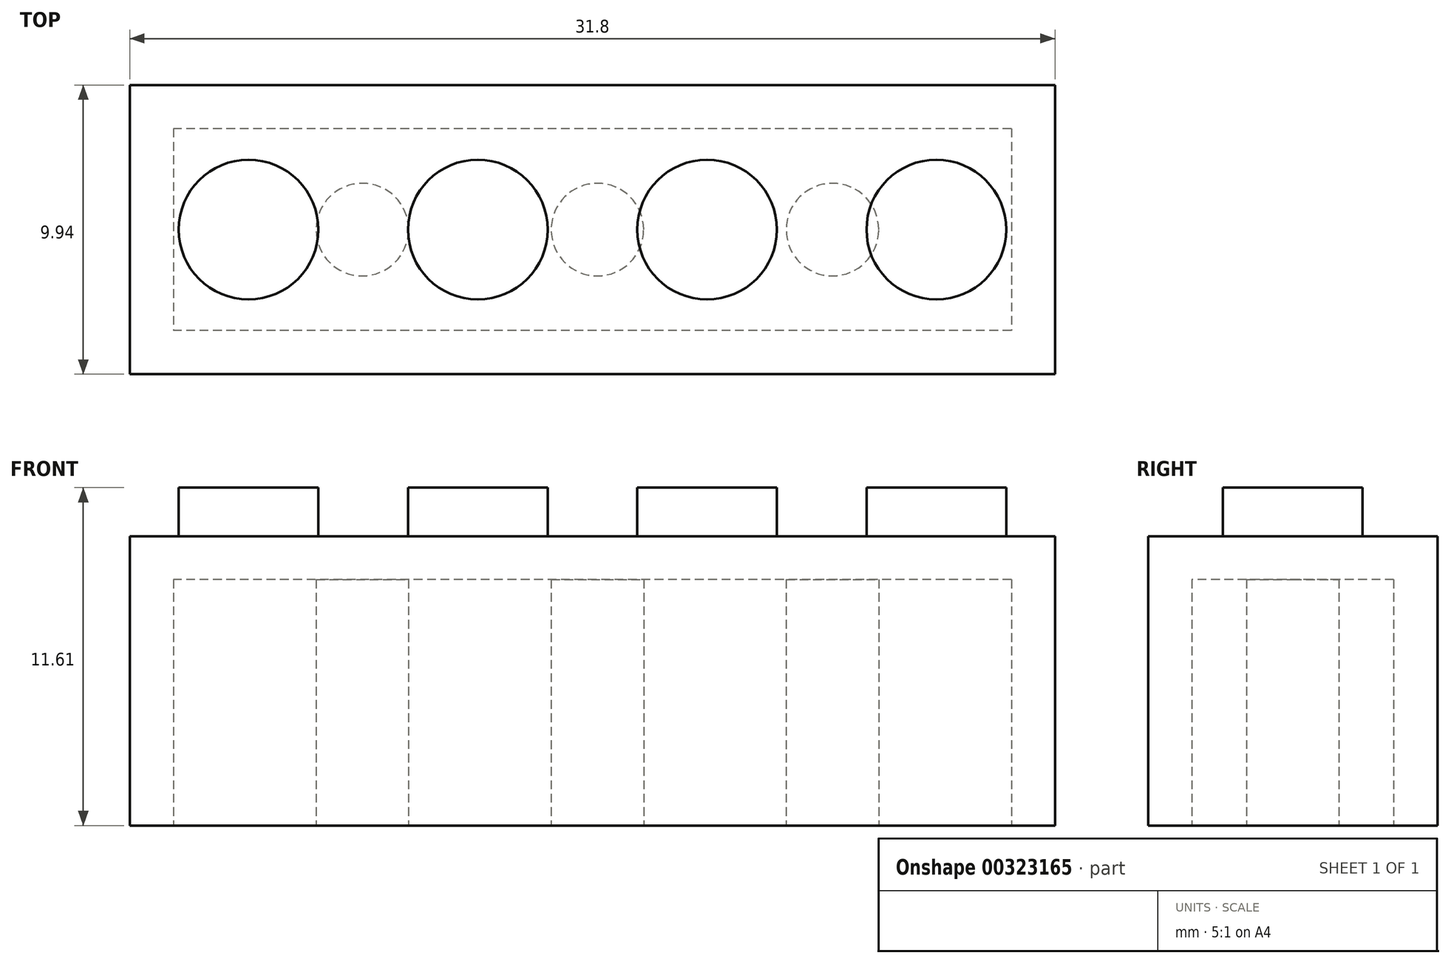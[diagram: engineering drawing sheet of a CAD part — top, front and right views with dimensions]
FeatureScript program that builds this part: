
annotation { "Feature Type Name" : "Feature", "Feature Type Description" : "" }
export const myFeature = defineFeature(function(context is Context, id is Id, definition is map)
    precondition{}
    {
        {
            var Q0;
            Q0=qCreatedBy(makeId("Top.planeOp"),FACE);
            var sketch = newSketch(context, id + "F0", { "sketchPlane" : qUnion([Q0])});
            skLineSegment(sketch, "E0.bottom", {"start": v(15.9, -4.97) * mm, "end": v(-15.9, -4.97) * mm});
            skLineSegment(sketch, "E0.top", {"start": v(15.9, 4.97) * mm, "end": v(-15.9, 4.97) * mm});
            skLineSegment(sketch, "E0.left", {"start": v(15.9, -4.97) * mm, "end": v(15.9, 4.97) * mm});
            skLineSegment(sketch, "E0.right", {"start": v(-15.9, -4.97) * mm, "end": v(-15.9, 4.97) * mm});
            skPoint(sketch, "E0.middle", {"position": v(0, 0) * mm});
            skCircle(sketch, "E1", {"center": v(-11.82, 0) * mm, "radius": 2.4 * mm});
            skCircle(sketch, "E2", {"center": v(-3.94, 0) * mm, "radius": 2.4 * mm});
            skCircle(sketch, "E3", {"center": v(3.94, 0) * mm, "radius": 2.4 * mm});
            skCircle(sketch, "E4", {"center": v(11.82, 0) * mm, "radius": 2.4 * mm});
            skSolve(sketch);
        }
        {
            var Q0;
            Q0=makeQuery(id+"F0.imprint","IMPRINT",FACE,{"disambiguationData":[TD([[makeQuery(id+"F0.imprint","IMPRINT",EDGE,{"derivedFrom":sQuery(id+"F0.wireOp",EDGE,"E0.bottom")}),-1.0]])]});
            var Q1;
            Q1=makeQuery(id+"F0.imprint","IMPRINT",FACE,{"disambiguationData":[TD([[makeQuery(id+"F0.imprint","IMPRINT",EDGE,{"derivedFrom":sQuery(id+"F0.wireOp",EDGE,"E1")}),1.0]])]});
            var Q2;
            Q2=makeQuery(id+"F0.imprint","IMPRINT",FACE,{"disambiguationData":[TD([[makeQuery(id+"F0.imprint","IMPRINT",EDGE,{"derivedFrom":sQuery(id+"F0.wireOp",EDGE,"E2")}),1.0]])]});
            var Q3;
            Q3=makeQuery(id+"F0.imprint","IMPRINT",FACE,{"disambiguationData":[TD([[makeQuery(id+"F0.imprint","IMPRINT",EDGE,{"derivedFrom":sQuery(id+"F0.wireOp",EDGE,"E3")}),1.0]])]});
            var Q4;
            Q4=makeQuery(id+"F0.imprint","IMPRINT",FACE,{"disambiguationData":[TD([[makeQuery(id+"F0.imprint","IMPRINT",EDGE,{"derivedFrom":sQuery(id+"F0.wireOp",EDGE,"E4")}),1.0]])]});
            extrude(context, id + "F1", {"entities" : qUnion([Q0, Q1, Q2, Q3, Q4]), "oppositeDirection" : true, "depth" : 9.94 * mm});
        }
        {
            var Q0;
            Q0=makeQuery(id+"F0.imprint","IMPRINT",FACE,{"disambiguationData":[TD([[makeQuery(id+"F0.imprint","IMPRINT",EDGE,{"derivedFrom":sQuery(id+"F0.wireOp",EDGE,"E1")}),1.0]])]});
            var Q1;
            Q1=makeQuery(id+"F0.imprint","IMPRINT",FACE,{"disambiguationData":[TD([[makeQuery(id+"F0.imprint","IMPRINT",EDGE,{"derivedFrom":sQuery(id+"F0.wireOp",EDGE,"E2")}),1.0]])]});
            var Q2;
            Q2=makeQuery(id+"F0.imprint","IMPRINT",FACE,{"disambiguationData":[TD([[makeQuery(id+"F0.imprint","IMPRINT",EDGE,{"derivedFrom":sQuery(id+"F0.wireOp",EDGE,"E3")}),1.0]])]});
            var Q3;
            Q3=makeQuery(id+"F0.imprint","IMPRINT",FACE,{"disambiguationData":[TD([[makeQuery(id+"F0.imprint","IMPRINT",EDGE,{"derivedFrom":sQuery(id+"F0.wireOp",EDGE,"E4")}),1.0]])]});
            extrude(context, id + "F2", {"entities" : qUnion([Q0, Q1, Q2, Q3]), "operationType" : NewBodyOperationType.ADD, "depth" : 1.67 * mm});
        }
        {
            var Q0;
            Q0=makeQuery(id+"F1.opExtrude","CAP_FACE",FACE,{"disambiguationData":[OSD([sQuery(id+"F0.wireOp",EDGE,"E0.bottom"),sQuery(id+"F0.wireOp",EDGE,"E0.top"),sQuery(id+"F0.wireOp",EDGE,"E0.left"),sQuery(id+"F0.wireOp",EDGE,"E0.right")])],"isStart":false});
            var sketch = newSketch(context, id + "F3", { "sketchPlane" : qUnion([Q0])});
            skLineSegment(sketch, "E5.bottom", {"start": v(14.4, -3.47) * mm, "end": v(-14.4, -3.47) * mm});
            skLineSegment(sketch, "E5.top", {"start": v(14.4, 3.47) * mm, "end": v(-14.4, 3.47) * mm});
            skLineSegment(sketch, "E5.left", {"start": v(14.4, -3.47) * mm, "end": v(14.4, 3.47) * mm});
            skLineSegment(sketch, "E5.right", {"start": v(-14.4, -3.47) * mm, "end": v(-14.4, 3.47) * mm});
            skPoint(sketch, "E5.middle", {"position": v(0, 0) * mm});
            skCircle(sketch, "E6", {"center": v(-7.9, 0) * mm, "radius": 1.59 * mm});
            skCircle(sketch, "E7", {"center": v(0.17, 0) * mm, "radius": 1.59 * mm});
            skCircle(sketch, "E8", {"center": v(8.25, 0) * mm, "radius": 1.59 * mm});
            skSolve(sketch);
        }
        {
            var Q0;
            Q0=makeQuery(id+"F3.imprint","IMPRINT",FACE,{"disambiguationData":[TD([[makeQuery(id+"F3.imprint","IMPRINT",EDGE,{"derivedFrom":sQuery(id+"F3.wireOp",EDGE,"E5.bottom")}),-1.0]])]});
            extrude(context, id + "F4", {"entities" : qUnion([Q0]), "operationType" : NewBodyOperationType.REMOVE, "oppositeDirection" : true, "depth" : 8.45 * mm});
        }
    });
